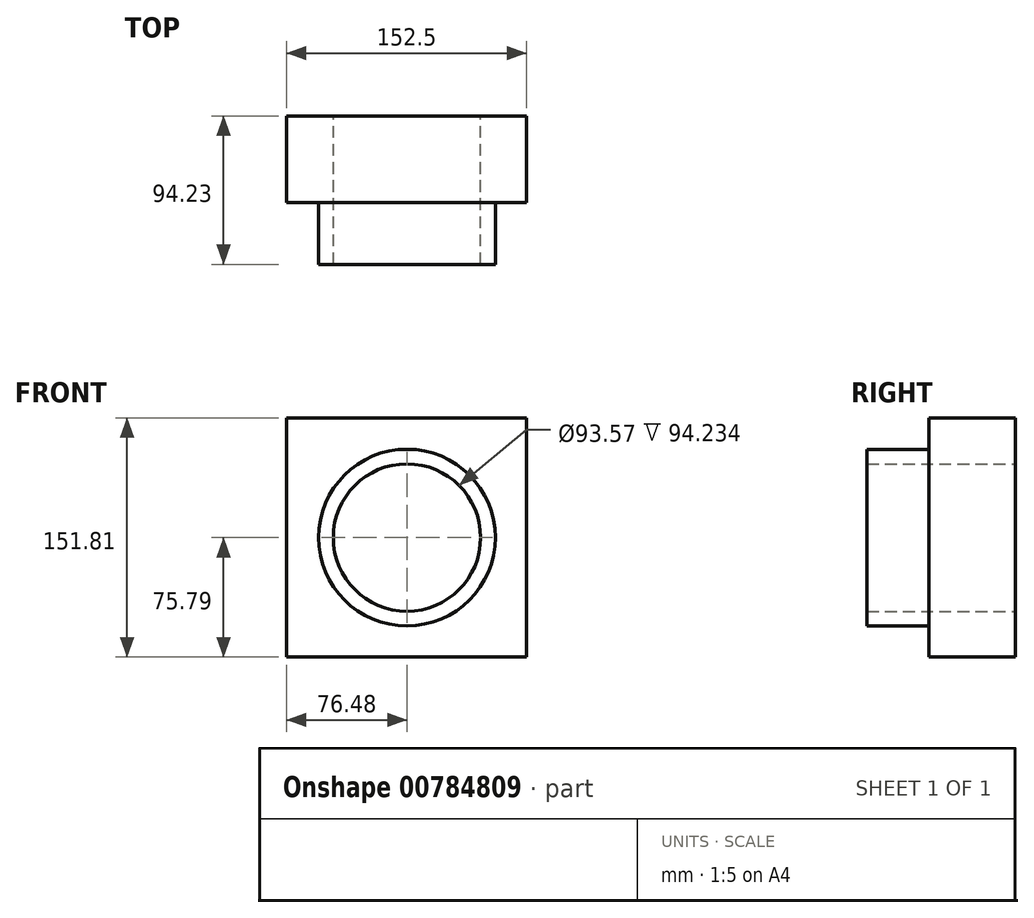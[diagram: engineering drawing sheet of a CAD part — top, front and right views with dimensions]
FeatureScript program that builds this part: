
annotation { "Feature Type Name" : "Feature", "Feature Type Description" : "" }
export const myFeature = defineFeature(function(context is Context, id is Id, definition is map)
    precondition{}
    {
        {
            var Q0;
            Q0=qCreatedBy(makeId("Front.planeOp"),FACE);
            var sketch = newSketch(context, id + "F0", { "sketchPlane" : qUnion([Q0])});
            skLineSegment(sketch, "E0.bottom", {"start": v(-76.48, 76.02) * mm, "end": v(76.02, 76.02) * mm});
            skLineSegment(sketch, "E0.top", {"start": v(-76.48, -75.8) * mm, "end": v(76.02, -75.8) * mm});
            skLineSegment(sketch, "E0.left", {"start": v(-76.48, 76.02) * mm, "end": v(-76.48, -75.8) * mm});
            skLineSegment(sketch, "E0.right", {"start": v(76.02, 76.02) * mm, "end": v(76.02, -75.8) * mm});
            skCircle(sketch, "E1", {"center": v(0, 0) * mm, "radius": 56.09 * mm});
            skCircle(sketch, "E2", {"center": v(0, 0) * mm, "radius": 46.78 * mm});
            skSolve(sketch);
        }
        {
            var Q0;
            Q0=makeQuery(id+"F0.imprint","IMPRINT",FACE,{"disambiguationData":[TD([[makeQuery(id+"F0.imprint","IMPRINT",EDGE,{"derivedFrom":sQuery(id+"F0.wireOp",EDGE,"E0.bottom")}),-1.0]])]});
            extrude(context, id + "F1", {"entities" : qUnion([Q0]), "depth" : 29.46 * mm, "offsetDistance" : 25.4 * mm});
        }
        {
            var Q0;
            Q0=makeQuery(id+"F0.imprint","IMPRINT",FACE,{"disambiguationData":[TD([[makeQuery(id+"F0.imprint","IMPRINT",EDGE,{"derivedFrom":sQuery(id+"F0.wireOp",EDGE,"E1")}),1.0]])]});
            extrude(context, id + "F2", {"entities" : qUnion([Q0]), "operationType" : NewBodyOperationType.ADD, "depth" : 68.83 * mm, "offsetDistance" : 25.4 * mm});
        }
        {
            var Q0;
            {var subQ0=sQuery(id+"F0.wireOp",EDGE,"E1");Q0=makeQuery(id+"F2.boolean.opBoolean","MERGE",FACE,{"derivedFrom":[makeQuery(id+"F1.opExtrude","CAP_FACE",FACE,{"disambiguationData":[OSD([sQuery(id+"F0.wireOp",EDGE,"E0.bottom"),sQuery(id+"F0.wireOp",EDGE,"E0.top"),sQuery(id+"F0.wireOp",EDGE,"E0.left"),sQuery(id+"F0.wireOp",EDGE,"E0.right"),subQ0])],"isStart":true}),makeQuery(id+"F2.opExtrude","CAP_FACE",FACE,{"disambiguationData":[OSD([subQ0,sQuery(id+"F0.wireOp",EDGE,"E2")])],"isStart":true})]});}
            extrude(context, id + "F3", {"entities" : qUnion([Q0]), "operationType" : NewBodyOperationType.ADD, "depth" : 25.4 * mm, "offsetDistance" : 25.4 * mm});
        }
    });
